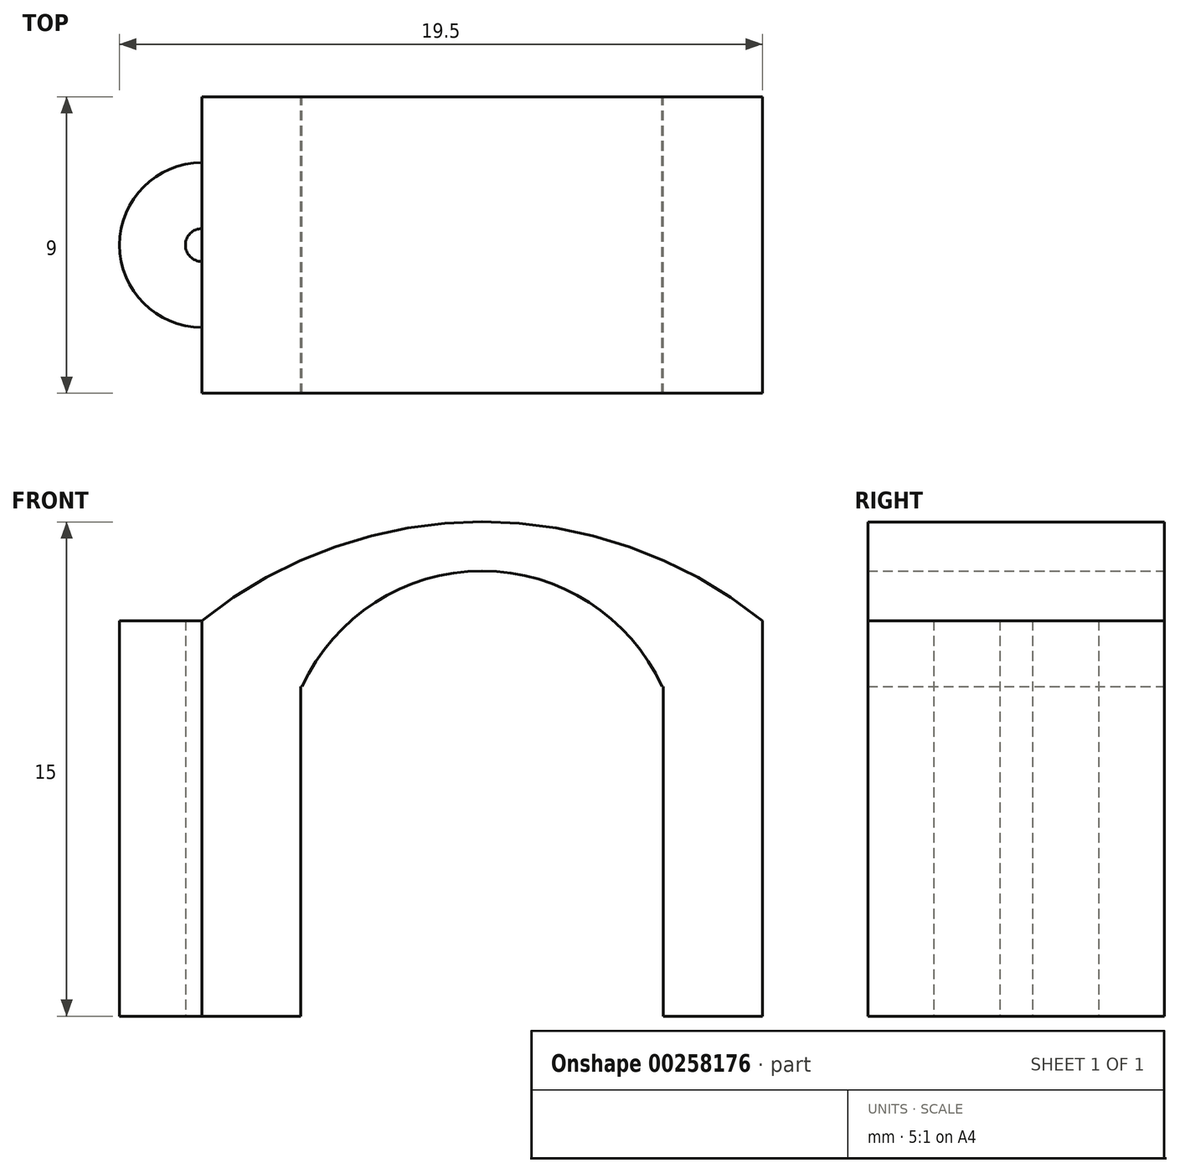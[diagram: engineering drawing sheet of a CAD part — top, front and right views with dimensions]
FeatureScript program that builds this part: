
annotation { "Feature Type Name" : "Feature", "Feature Type Description" : "" }
export const myFeature = defineFeature(function(context is Context, id is Id, definition is map)
    precondition{}
    {
        {
            var Q0;
            Q0=qCreatedBy(makeId("Front.planeOp"),FACE);
            var sketch = newSketch(context, id + "F0", { "sketchPlane" : qUnion([Q0])});
            skLineSegment(sketch, "E0", {"start": v(0, 0) * mm, "end": v(17, 0) * mm});
            skLineSegment(sketch, "E1", {"start": v(0, 0) * mm, "end": v(0, 12) * mm});
            skLineSegment(sketch, "E2", {"start": v(17, 0) * mm, "end": v(17, 12) * mm});
            skLineSegment(sketch, "E3", {"start": v(8.5, 0) * mm, "end": v(8.5, 15) * mm, "construction": true});
            skArc(sketch, "E4", {"start": v(17, 12) * mm, "mid": v(8.5, 15) * mm, "end": v(0, 12) * mm});
            skLineSegment(sketch, "E5", {"start": v(0, 0) * mm, "end": v(3, 0) * mm});
            skLineSegment(sketch, "E6", {"start": v(3, 0) * mm, "end": v(3, 10) * mm});
            skLineSegment(sketch, "E7.MirrorCS", {"start": v(14, 0) * mm, "end": v(14, 10) * mm});
            skLineSegment(sketch, "E8", {"start": v(3, 10) * mm, "end": v(3.04, 10) * mm});
            skArc(sketch, "E9", {"start": v(14, 9.92) * mm, "mid": v(8.5, 13.5) * mm, "end": v(3, 9.92) * mm});
            skLineSegment(sketch, "E10.trimOffspring", {"start": v(13.96, 10) * mm, "end": v(14, 10) * mm});
            skSolve(sketch);
        }
        {
            var Q0;
            Q0=makeQuery(id+"F0.imprint","IMPRINT",FACE,{"disambiguationData":[TD([[makeQuery(id+"F0.imprint","IMPRINT",EDGE,{"derivedFrom":sQuery(id+"F0.wireOp",EDGE,"E1")}),-1.0]])]});
            extrude(context, id + "F1", {"entities" : qUnion([Q0]), "depth" : 9 * mm});
        }
        {
            var Q0;
            Q0=qCreatedBy(makeId("Top.planeOp"),FACE);
            var sketch = newSketch(context, id + "F2", { "sketchPlane" : qUnion([Q0])});
            skLineSegment(sketch, "E11.0", {"start": v(0, -9) * mm, "end": v(0, 0) * mm});
            skLineSegment(sketch, "E12.0", {"start": v(17, 0) * mm, "end": v(0, 0) * mm});
            skLineSegment(sketch, "E13.0", {"start": v(17, -9) * mm, "end": v(0, -9) * mm});
            skLineSegment(sketch, "E14.0", {"start": v(17, -9) * mm, "end": v(17, 0) * mm});
            skCircle(sketch, "E15", {"center": v(0, -4.5) * mm, "radius": 2.5 * mm});
            skCircle(sketch, "E16", {"center": v(0, -4.5) * mm, "radius": 0.5 * mm});
            skSolve(sketch);
        }
        {
            var Q0;
            {var subQ0=sQuery(id+"F2.wireOp",EDGE,"E15");var subQ1=sQuery(id+"F2.wireOp",EDGE,"E11.0");var subQ2=makeQuery(id+"F2.imprint","INTERSECT",VERTEX,{"disambiguationData":[OD(0.0)],"derivedFrom":[subQ1,subQ0]});Q0=makeQuery(id+"F2.imprint","IMPRINT",FACE,{"disambiguationData":[TD([[makeQuery(id+"F2.imprint","IMPRINT",EDGE,{"disambiguationData":[TD([[subQ2,-1.0]])],"derivedFrom":subQ1}),1.0]])]});}
            extrude(context, id + "F3", {"entities" : qUnion([Q0]), "operationType" : NewBodyOperationType.ADD, "depth" : 12 * mm});
        }
    });
